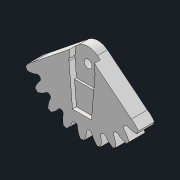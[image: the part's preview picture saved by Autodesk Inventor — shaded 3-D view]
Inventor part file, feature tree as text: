
AUTODESK INVENTOR PART (.ipt)
format: ipt  version: 2022.2 (Build 262287010, 287A)  size: 332,288 bytes
history: native  units: mm
features: extrude x6, sketch x4, other x3, reference x2, pattern_circular x1, imported_body x1, boolean_combine x1, plane x1, projected_geometry x1
ambient origin geometry x8: Origin, YZ Plane, XZ Plane, XY Plane, X Axis, Y Axis, Z Axis, Center Point
bodies: Solid1 (feature_tree), Solid3 (feature_tree)
feature tree (20):
  sketch  "Sketch1"  dims[d0=8.0mm d1=0.0mm]
  extrude  "Extrusion1"  TaperAngle=0.0deg  [1 undecoded]
  extrude  "Extrusion2"  Depth=230.0mm TaperAngle=360.0deg
  pattern_circular  "Circular Pattern1"  Angle=120.0deg  [1 undecoded]
  extrude  "Extrusion4"  Depth=2.0mm
  extrude  "Extrusion5"  TaperAngle=0.0deg  [1 undecoded]
  imported_body  "Base2"
  extrude  "Extrusion9"  TaperAngle=0.0deg  [1 undecoded]
  boolean_combine  "Combine1"
  plane  "Work Plane2"
  extrude  "Extrusion11"  Depth=10.0mm TaperAngle=0.0deg
  sketch  "Sketch3"  dims[d2=0.0mm d3=0.0mm d4=230.0mm d5=360.0deg]
  sketch  "Sketch4"  dims[d16=4.0mm]
  projected_geometry  "Projected Loop1"
  sketch  "Sketch8"  dims[d17=0.0mm d18=0.0mm d19=120.0deg d20=15.0mm d21=0.0mm d22=0.0mm d51=0.0mm d52=0.0mm d59=10.0mm d60=0.0mm d61=2.0mm]
  reference  "Reference6"
  reference  "Reference7"
  parser-record x1  (decoder bookkeeping rows leaked as tree rows — omitted from the tree; the rows remain in map.json)
  other  "HydrolicDriver.iam"
  other  "NyArm:1"
note: 4 required parameter values undecoded (feature->parameter linkage not recoverable at this tier; creation-order binding heuristic only, values carry confidence <= 0.55)
note: 1 file-system path scrubbed to <path> (originals preserved in map.json)
